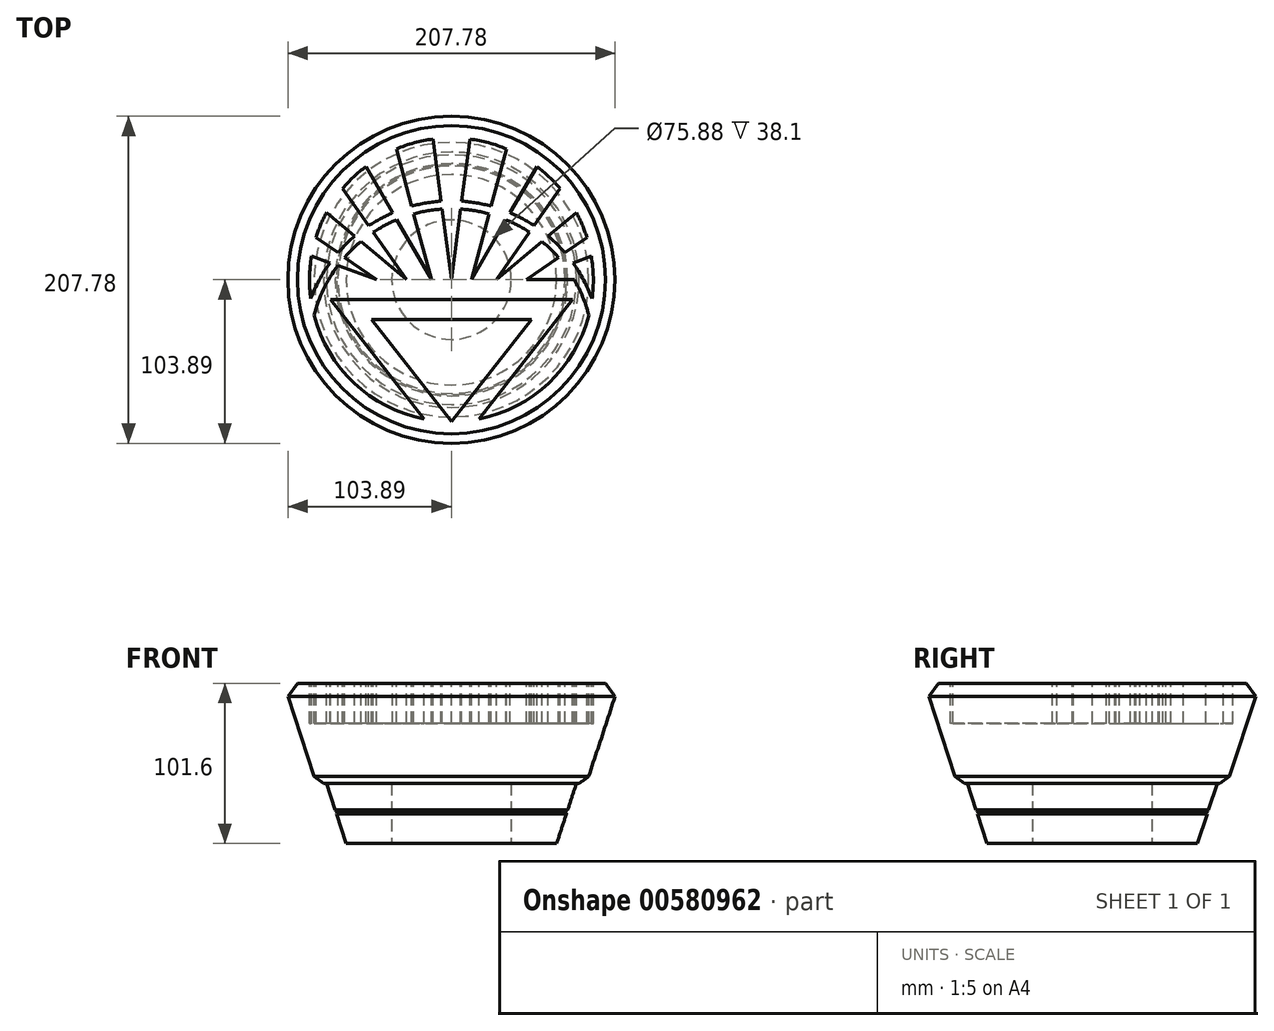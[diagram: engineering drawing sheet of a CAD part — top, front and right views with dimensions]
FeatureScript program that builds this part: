
annotation { "Feature Type Name" : "Feature", "Feature Type Description" : "" }
export const myFeature = defineFeature(function(context is Context, id is Id, definition is map)
    precondition{}
    {
        {
            var Q0;
            Q0=qCreatedBy(makeId("Top.planeOp"),FACE);
            var sketch = newSketch(context, id + "F0", { "sketchPlane" : qUnion([Q0])});
            skCircle(sketch, "E0", {"center": v(0, 0) * mm, "radius": 66.85 * mm});
            skSolve(sketch);
        }
        {
            var Q0;
            Q0=qCreatedBy(makeId("Top.planeOp"),FACE);
            cPlane(context, id + "F1", {"entities" : qUnion([Q0]), "cplaneType" : CPlaneType.OFFSET, "offset" : 101.6 * mm, "width" : 152.4 * mm, "height" : 152.4 * mm});
        }
        {
            var Q0;
            Q0=qCreatedBy(id+"F1.planeOp",FACE);
            var sketch = newSketch(context, id + "F2", { "sketchPlane" : qUnion([Q0])});
            skCircle(sketch, "E1", {"center": v(0, 0) * mm, "radius": 100.28 * mm});
            skSolve(sketch);
        }
        {
            var Q0;
            Q0=makeQuery(id+"F2.imprint","IMPRINT",FACE,{"disambiguationData":[TD([[makeQuery(id+"F2.imprint","IMPRINT",EDGE,{"derivedFrom":sQuery(id+"F2.wireOp",EDGE,"E1")}),1.0]])]});
            var Q1;
            Q1=makeQuery(id+"F0.imprint","IMPRINT",FACE,{"disambiguationData":[TD([[makeQuery(id+"F0.imprint","IMPRINT",EDGE,{"derivedFrom":sQuery(id+"F0.wireOp",EDGE,"E0")}),1.0]])]});
            var Q2;
            Q2=sQuery(id+"F2.wireOp",EDGE,"Eyu8YDiN-lEGU-Wuxt-0ncA-RZLAWeJK4OgB");
            var Q3;
            Q3=sQuery(id+"F0.wireOp",EDGE,"fgfE4CqQ-t5n6-ucAx-yhIW-5wF2yx0Jya2k");
            loft(context, id + "F3", {"sheetProfilesArray" : [{ "sheetProfileEntities" : qUnion([Q0]) }, { "sheetProfileEntities" : qUnion([Q1]) }], "wireProfilesArray" : [{ "wireProfileEntities" : qUnion([Q2]) }, { "wireProfileEntities" : qUnion([Q3]) }]});
        }
        {
            var Q0;
            Q0=qCreatedBy(makeId("Top.planeOp"),FACE);
            var sketch = newSketch(context, id + "F4", { "sketchPlane" : qUnion([Q0])});
            skCircle(sketch, "E2", {"center": v(0, 0) * mm, "radius": 37.94 * mm});
            skSolve(sketch);
        }
        {
            var Q0;
            Q0=makeQuery(id+"F4.imprint","IMPRINT",FACE,{"disambiguationData":[TD([[makeQuery(id+"F4.imprint","IMPRINT",EDGE,{"derivedFrom":sQuery(id+"F4.wireOp",EDGE,"E2")}),1.0]])]});
            extrude(context, id + "F5", {"entities" : qUnion([Q0]), "operationType" : NewBodyOperationType.REMOVE, "depth" : 53.34 * mm, "offsetDistance" : 25.4 * mm});
        }
        {
            var Q0;
            Q0=qCreatedBy(makeId("Top.planeOp"),FACE);
            cPlane(context, id + "F6", {"entities" : qUnion([Q0]), "cplaneType" : CPlaneType.OFFSET, "offset" : 38.1 * mm, "width" : 152.4 * mm, "height" : 152.4 * mm});
        }
        {
            var Q0;
            Q0=qCreatedBy(id+"F6.planeOp",FACE);
            var sketch = newSketch(context, id + "F7", { "sketchPlane" : qUnion([Q0])});
            skCircle(sketch, "E3", {"center": v(0, 0) * mm, "radius": 85.73 * mm});
            skSolve(sketch);
        }
        {
            var Q0;
            Q0=qCreatedBy(id+"F1.planeOp",FACE);
            var sketch = newSketch(context, id + "F8", { "sketchPlane" : qUnion([Q0])});
            skCircle(sketch, "E4", {"center": v(0, 0) * mm, "radius": 106.63 * mm});
            skSolve(sketch);
        }
        {
            var Q1;
            Q1=makeQuery(id+"F7.imprint","IMPRINT",FACE,{"disambiguationData":[TD([[makeQuery(id+"F7.imprint","IMPRINT",EDGE,{"derivedFrom":sQuery(id+"F7.wireOp",EDGE,"E3")}),1.0]])]});
            var Q2;
            Q2=makeQuery(id+"F8.imprint","IMPRINT",FACE,{"disambiguationData":[TD([[makeQuery(id+"F8.imprint","IMPRINT",EDGE,{"derivedFrom":sQuery(id+"F8.wireOp",EDGE,"E4")}),1.0]])]});
            loft(context, id + "F9", {"operationType" : NewBodyOperationType.ADD, "sheetProfilesArray" : [{ "sheetProfileEntities" : qUnion([Q1]) }, { "sheetProfileEntities" : qUnion([Q2]) }]});
        }
        {
            var Q0;
            Q0=makeQuery(id+"F9.opLoft","MID_CAP_EDGE",EDGE,{"disambiguationData":[OSD([sQuery(id+"F7.wireOp",EDGE,"E3")])],"capPos":0.0});
            chamfer(context, id + "F10", {"entities" : qUnion([Q0]), "width" : 6.35 * mm, "tangentPropagation" : true});
        }
        {
            var Q0;
            Q0=makeQuery(id+"F9.opLoft","MID_CAP_EDGE",EDGE,{"disambiguationData":[OSD([sQuery(id+"F7.wireOp",EDGE,"E3"),sQuery(id+"F8.wireOp",EDGE,"E4")])],"capPos":1.0});
            chamfer(context, id + "F11", {"entities" : qUnion([Q0]), "width" : 6.35 * mm, "tangentPropagation" : true});
        }
        {
            var Q0;
            Q0=qCreatedBy(makeId("Front.planeOp"),FACE);
            var sketch = newSketch(context, id + "F12", { "sketchPlane" : qUnion([Q0])});
            skLineSegment(sketch, "E5", {"start": v(-79.4, 38.11) * mm, "end": v(-66.85, 0) * mm});
            skLineSegment(sketch, "E6", {"start": v(-73.8, 21.14) * mm, "end": v(-72.2, 20.33) * mm});
            skLineSegment(sketch, "E7", {"start": v(-72.2, 20.33) * mm, "end": v(-73.02, 18.73) * mm});
            skSolve(sketch);
        }
        {
            var Q0;
            Q0=qCreatedBy(makeId("Right.planeOp"),FACE);
            var sketch = newSketch(context, id + "F13", { "sketchPlane" : qUnion([Q0])});
            skLineSegment(sketch, "E8", {"start": v(0, 0) * mm, "end": v(0, 184.2) * mm});
            skSolve(sketch);
        }
        {
            var Q0;
            Q0=qSketchRegion(id+"F12",true);
            var Q1;
            Q1=sQuery(id+"F13.wireOp",EDGE,"E8");
            revolve(context, id + "F14", {"operationType" : NewBodyOperationType.REMOVE, "entities" : qUnion([Q0]), "axis" : qUnion([Q1]), "revolveType" : RevolveType.FULL, "oppositeDirection" : true});
        }
        {
            var Q0;
            Q0=makeQuery(id+"F9.boolean.opBoolean","MERGE",FACE,{"derivedFrom":[makeQuery(id+"F3.opLoft","CAP_FACE",FACE,{"disambiguationData":[OSD([makeQuery(id+"F2.imprint","IMPRINT",FACE,{"disambiguationData":[TD([[makeQuery(id+"F2.imprint","IMPRINT",EDGE,{"derivedFrom":sQuery(id+"F2.wireOp",EDGE,"E1")}),1.0]])]})])],"isStart":true}),makeQuery(id+"F9.opLoft","CAP_FACE",FACE,{"disambiguationData":[OSD([makeQuery(id+"F8.imprint","IMPRINT",FACE,{"disambiguationData":[TD([[makeQuery(id+"F8.imprint","IMPRINT",EDGE,{"derivedFrom":sQuery(id+"F8.wireOp",EDGE,"E4")}),1.0]])]})])],"isStart":true})]});
            var sketch = newSketch(context, id + "F15", { "sketchPlane" : qUnion([Q0])});
            skCircle(sketch, "E9", {"center": v(0, 0) * mm, "radius": 100.28 * mm});
            skCircle(sketch, "E10.0", {"center": v(0, 0) * mm, "radius": 90.12 * mm});
            skLineSegment(sketch, "E11", {"start": v(0, 0) * mm, "end": v(0, 0) * mm});
            skLineSegment(sketch, "E12", {"start": v(0, -25.4) * mm, "end": v(-50.8, -25.4) * mm});
            skLineSegment(sketch, "E13", {"start": v(-50.8, -25.4) * mm, "end": v(0, -90.12) * mm});
            skLineSegment(sketch, "E14.0", {"start": v(-76.91, -12.7) * mm, "end": v(-17.49, -88.4) * mm});
            skLineSegment(sketch, "E14.1", {"start": v(0, -12.7) * mm, "end": v(-76.91, -12.7) * mm});
            skLineSegment(sketch, "E15.MirrorCS", {"start": v(0, -12.7) * mm, "end": v(76.91, -12.7) * mm});
            skLineSegment(sketch, "E16.MirrorCS", {"start": v(0, -25.4) * mm, "end": v(50.8, -25.4) * mm});
            skLineSegment(sketch, "E17.MirrorCS", {"start": v(50.8, -25.4) * mm, "end": v(0, -90.12) * mm});
            skLineSegment(sketch, "E18.MirrorCS", {"start": v(76.91, -12.7) * mm, "end": v(17.49, -88.4) * mm});
            skCircle(sketch, "E19", {"center": v(0, -45.06) * mm, "radius": 90.12 * mm});
            skLineSegment(sketch, "E20", {"start": v(0, 45.06) * mm, "end": v(0, 90.12) * mm});
            skLineSegment(sketch, "E21", {"start": v(0, 45.06) * mm, "end": v(0, 0) * mm});
            skLineSegment(sketch, "E22", {"start": v(0, 0) * mm, "end": v(0, -45.06) * mm});
            skCircle(sketch, "E23", {"center": v(0, -45.06) * mm, "radius": 95.2 * mm});
            skLineSegment(sketch, "E24", {"start": v(0, 0) * mm, "end": v(-11.76, 89.35) * mm});
            skLineSegment(sketch, "E25", {"start": v(0, 0) * mm, "end": v(11.76, 89.35) * mm});
            skLineSegment(sketch, "E26", {"start": v(-90.12, 0) * mm, "end": v(90.12, 0) * mm});
            skLineSegment(sketch, "E27", {"start": v(-12.7, 0) * mm, "end": v(-34.96, 83.06) * mm});
            skLineSegment(sketch, "E28", {"start": v(-12.7, 0) * mm, "end": v(-54.25, 71.96) * mm});
            skLineSegment(sketch, "E29", {"start": v(-28.57, 0) * mm, "end": v(-69.1, 57.86) * mm});
            skLineSegment(sketch, "E30", {"start": v(-28.58, 0) * mm, "end": v(-79.4, 42.64) * mm});
            skLineSegment(sketch, "E31", {"start": v(-47.62, 0) * mm, "end": v(-86.02, 26.88) * mm});
            skLineSegment(sketch, "E32", {"start": v(-47.62, 0) * mm, "end": v(-88.86, 15) * mm});
            skLineSegment(sketch, "E33.MirrorCS", {"start": v(12.7, 0) * mm, "end": v(34.96, 83.06) * mm});
            skLineSegment(sketch, "E34.MirrorCS", {"start": v(12.7, 0) * mm, "end": v(54.25, 71.96) * mm});
            skLineSegment(sketch, "E35.MirrorCS", {"start": v(28.57, 0) * mm, "end": v(69.1, 57.86) * mm});
            skLineSegment(sketch, "E36.MirrorCS", {"start": v(28.57, 0) * mm, "end": v(79.4, 42.64) * mm});
            skLineSegment(sketch, "E37.MirrorCS", {"start": v(47.62, 0) * mm, "end": v(86.02, 26.88) * mm});
            skLineSegment(sketch, "E38.MirrorCS", {"start": v(47.62, 0) * mm, "end": v(88.86, 15) * mm});
            skSolve(sketch);
        }
        {
            var Q0;
            Q0=makeQuery(id+"F15.imprint","IMPRINT",FACE,{"disambiguationData":[TD([[makeQuery(id+"F15.imprint","IMPRINT",EDGE,{"derivedFrom":sQuery(id+"F15.wireOp",EDGE,"E12")}),1.0]])]});
            var Q1;
            {var subQ6=sQuery(id+"F15.wireOp",EDGE,"E14.0");Q1=makeQuery(id+"F15.imprint","IMPRINT",FACE,{"disambiguationData":[TD([[makeQuery(id+"F15.imprint","IMPRINT",EDGE,{"derivedFrom":subQ6}),-1.0]])]});}
            var Q2;
            {var subQ5=sQuery(id+"F15.wireOp",EDGE,"E15.MirrorCS");Q2=makeQuery(id+"F15.imprint","IMPRINT",FACE,{"disambiguationData":[TD([[makeQuery(id+"F15.imprint","IMPRINT",EDGE,{"derivedFrom":subQ5}),1.0]])]});}
            var Q3;
            {var subQ0=sQuery(id+"F15.wireOp",EDGE,"E26");var subQ1=sQuery(id+"F15.wireOp",EDGE,"E10.0");var subQ2=makeQuery(id+"F15.imprint","INTERSECT",VERTEX,{"disambiguationData":[OD(0.0)],"derivedFrom":[subQ1,subQ0]});Q3=makeQuery(id+"F15.imprint","IMPRINT",FACE,{"disambiguationData":[TD([[makeQuery(id+"F15.imprint","IMPRINT",EDGE,{"disambiguationData":[TD([[subQ2,-1.0]])],"derivedFrom":subQ1}),1.0]])]});}
            var Q4;
            {var subQ0=sQuery(id+"F15.wireOp",EDGE,"E26");var subQ1=sQuery(id+"F15.wireOp",EDGE,"E10.0");var subQ2=makeQuery(id+"F15.imprint","INTERSECT",VERTEX,{"disambiguationData":[OD(0.0)],"derivedFrom":[subQ1,subQ0]});Q4=makeQuery(id+"F15.imprint","IMPRINT",FACE,{"disambiguationData":[TD([[makeQuery(id+"F15.imprint","IMPRINT",EDGE,{"disambiguationData":[TD([[subQ2,1.0]])],"derivedFrom":subQ1}),1.0]])]});}
            var Q5;
            {var subQ0=sQuery(id+"F15.wireOp",EDGE,"E32");var subQ1=sQuery(id+"F15.wireOp",EDGE,"E19");var subQ2=makeQuery(id+"F15.imprint","INTERSECT",VERTEX,{"derivedFrom":[subQ1,subQ0]});Q5=makeQuery(id+"F15.imprint","IMPRINT",FACE,{"disambiguationData":[TD([[makeQuery(id+"F15.imprint","IMPRINT",EDGE,{"disambiguationData":[TD([[subQ2,-1.0]])],"derivedFrom":subQ1}),1.0]])]});}
            var Q6;
            {var subQ0=sQuery(id+"F15.wireOp",EDGE,"E30");var subQ1=sQuery(id+"F15.wireOp",EDGE,"E19");var subQ2=makeQuery(id+"F15.imprint","INTERSECT",VERTEX,{"derivedFrom":[subQ1,subQ0]});Q6=makeQuery(id+"F15.imprint","IMPRINT",FACE,{"disambiguationData":[TD([[makeQuery(id+"F15.imprint","IMPRINT",EDGE,{"disambiguationData":[TD([[subQ2,-1.0]])],"derivedFrom":subQ1}),1.0]])]});}
            var Q7;
            {var subQ0=sQuery(id+"F15.wireOp",EDGE,"E30");var subQ1=sQuery(id+"F15.wireOp",EDGE,"E10.0");var subQ2=makeQuery(id+"F15.imprint","INTERSECT",VERTEX,{"derivedFrom":[subQ1,subQ0]});Q7=makeQuery(id+"F15.imprint","IMPRINT",FACE,{"disambiguationData":[TD([[makeQuery(id+"F15.imprint","IMPRINT",EDGE,{"disambiguationData":[TD([[subQ2,-1.0]])],"derivedFrom":subQ1}),1.0]])]});}
            var Q8;
            {var subQ0=sQuery(id+"F15.wireOp",EDGE,"E28");var subQ1=sQuery(id+"F15.wireOp",EDGE,"E10.0");var subQ2=makeQuery(id+"F15.imprint","INTERSECT",VERTEX,{"derivedFrom":[subQ1,subQ0]});Q8=makeQuery(id+"F15.imprint","IMPRINT",FACE,{"disambiguationData":[TD([[makeQuery(id+"F15.imprint","IMPRINT",EDGE,{"disambiguationData":[TD([[subQ2,-1.0]])],"derivedFrom":subQ1}),1.0]])]});}
            var Q9;
            {var subQ0=sQuery(id+"F15.wireOp",EDGE,"E28");var subQ1=sQuery(id+"F15.wireOp",EDGE,"E19");var subQ2=makeQuery(id+"F15.imprint","INTERSECT",VERTEX,{"derivedFrom":[subQ1,subQ0]});Q9=makeQuery(id+"F15.imprint","IMPRINT",FACE,{"disambiguationData":[TD([[makeQuery(id+"F15.imprint","IMPRINT",EDGE,{"disambiguationData":[TD([[subQ2,-1.0]])],"derivedFrom":subQ1}),1.0]])]});}
            var Q10;
            {var subQ0=sQuery(id+"F15.wireOp",EDGE,"E24");var subQ1=sQuery(id+"F15.wireOp",EDGE,"E10.0");var subQ2=makeQuery(id+"F15.imprint","INTERSECT",VERTEX,{"derivedFrom":[subQ1,subQ0]});Q10=makeQuery(id+"F15.imprint","IMPRINT",FACE,{"disambiguationData":[TD([[makeQuery(id+"F15.imprint","IMPRINT",EDGE,{"disambiguationData":[TD([[subQ2,-1.0]])],"derivedFrom":subQ1}),1.0]])]});}
            var Q11;
            {var subQ0=sQuery(id+"F15.wireOp",EDGE,"E24");var subQ1=sQuery(id+"F15.wireOp",EDGE,"E19");var subQ2=makeQuery(id+"F15.imprint","INTERSECT",VERTEX,{"derivedFrom":[subQ1,subQ0]});Q11=makeQuery(id+"F15.imprint","IMPRINT",FACE,{"disambiguationData":[TD([[makeQuery(id+"F15.imprint","IMPRINT",EDGE,{"disambiguationData":[TD([[subQ2,-1.0]])],"derivedFrom":subQ1}),1.0]])]});}
            var Q12;
            {var subQ0=sQuery(id+"F15.wireOp",EDGE,"E33.MirrorCS");var subQ1=sQuery(id+"F15.wireOp",EDGE,"E19");var subQ2=makeQuery(id+"F15.imprint","INTERSECT",VERTEX,{"derivedFrom":[subQ1,subQ0]});Q12=makeQuery(id+"F15.imprint","IMPRINT",FACE,{"disambiguationData":[TD([[makeQuery(id+"F15.imprint","IMPRINT",EDGE,{"disambiguationData":[TD([[subQ2,-1.0]])],"derivedFrom":subQ1}),1.0]])]});}
            var Q13;
            {var subQ0=sQuery(id+"F15.wireOp",EDGE,"E25");var subQ1=sQuery(id+"F15.wireOp",EDGE,"E10.0");var subQ2=makeQuery(id+"F15.imprint","INTERSECT",VERTEX,{"derivedFrom":[subQ1,subQ0]});Q13=makeQuery(id+"F15.imprint","IMPRINT",FACE,{"disambiguationData":[TD([[makeQuery(id+"F15.imprint","IMPRINT",EDGE,{"disambiguationData":[TD([[subQ2,1.0]])],"derivedFrom":subQ1}),1.0]])]});}
            var Q14;
            {var subQ0=sQuery(id+"F15.wireOp",EDGE,"E35.MirrorCS");var subQ1=sQuery(id+"F15.wireOp",EDGE,"E19");var subQ2=makeQuery(id+"F15.imprint","INTERSECT",VERTEX,{"derivedFrom":[subQ1,subQ0]});Q14=makeQuery(id+"F15.imprint","IMPRINT",FACE,{"disambiguationData":[TD([[makeQuery(id+"F15.imprint","IMPRINT",EDGE,{"disambiguationData":[TD([[subQ2,-1.0]])],"derivedFrom":subQ1}),1.0]])]});}
            var Q15;
            {var subQ0=sQuery(id+"F15.wireOp",EDGE,"E37.MirrorCS");var subQ1=sQuery(id+"F15.wireOp",EDGE,"E19");var subQ2=makeQuery(id+"F15.imprint","INTERSECT",VERTEX,{"derivedFrom":[subQ1,subQ0]});Q15=makeQuery(id+"F15.imprint","IMPRINT",FACE,{"disambiguationData":[TD([[makeQuery(id+"F15.imprint","IMPRINT",EDGE,{"disambiguationData":[TD([[subQ2,-1.0]])],"derivedFrom":subQ1}),1.0]])]});}
            var Q16;
            {var subQ0=sQuery(id+"F15.wireOp",EDGE,"E36.MirrorCS");var subQ1=sQuery(id+"F15.wireOp",EDGE,"E10.0");var subQ2=makeQuery(id+"F15.imprint","INTERSECT",VERTEX,{"derivedFrom":[subQ1,subQ0]});Q16=makeQuery(id+"F15.imprint","IMPRINT",FACE,{"disambiguationData":[TD([[makeQuery(id+"F15.imprint","IMPRINT",EDGE,{"disambiguationData":[TD([[subQ2,1.0]])],"derivedFrom":subQ1}),1.0]])]});}
            var Q17;
            {var subQ0=sQuery(id+"F15.wireOp",EDGE,"E26");var subQ1=sQuery(id+"F15.wireOp",EDGE,"E10.0");var subQ2=makeQuery(id+"F15.imprint","INTERSECT",VERTEX,{"disambiguationData":[OD(1.0)],"derivedFrom":[subQ1,subQ0]});Q17=makeQuery(id+"F15.imprint","IMPRINT",FACE,{"disambiguationData":[TD([[makeQuery(id+"F15.imprint","IMPRINT",EDGE,{"disambiguationData":[TD([[subQ2,-1.0]])],"derivedFrom":subQ1}),1.0]])]});}
            var Q18;
            {var subQ0=sQuery(id+"F15.wireOp",EDGE,"E26");var subQ1=sQuery(id+"F15.wireOp",EDGE,"E19");var subQ2=makeQuery(id+"F15.imprint","INTERSECT",VERTEX,{"disambiguationData":[OD(0.0)],"derivedFrom":[subQ1,subQ0]});Q18=makeQuery(id+"F15.imprint","IMPRINT",FACE,{"disambiguationData":[TD([[makeQuery(id+"F15.imprint","IMPRINT",EDGE,{"disambiguationData":[TD([[subQ2,-1.0]])],"derivedFrom":subQ1}),1.0]])]});}
            var Q19;
            {var subQ0=sQuery(id+"F15.wireOp",EDGE,"E26");var subQ1=sQuery(id+"F15.wireOp",EDGE,"E10.0");var subQ2=makeQuery(id+"F15.imprint","INTERSECT",VERTEX,{"disambiguationData":[OD(1.0)],"derivedFrom":[subQ1,subQ0]});Q19=makeQuery(id+"F15.imprint","IMPRINT",FACE,{"disambiguationData":[TD([[makeQuery(id+"F15.imprint","IMPRINT",EDGE,{"disambiguationData":[TD([[subQ2,1.0]])],"derivedFrom":subQ1}),1.0]])]});}
            var Q20;
            {var subQ0=sQuery(id+"F15.wireOp",EDGE,"E34.MirrorCS");var subQ1=sQuery(id+"F15.wireOp",EDGE,"E10.0");var subQ2=makeQuery(id+"F15.imprint","INTERSECT",VERTEX,{"derivedFrom":[subQ1,subQ0]});Q20=makeQuery(id+"F15.imprint","IMPRINT",FACE,{"disambiguationData":[TD([[makeQuery(id+"F15.imprint","IMPRINT",EDGE,{"disambiguationData":[TD([[subQ2,1.0]])],"derivedFrom":subQ1}),1.0]])]});}
            extrude(context, id + "F16", {"entities" : qUnion([Q0, Q1, Q2, Q3, Q4, Q5, Q6, Q7, Q8, Q9, Q10, Q11, Q12, Q13, Q14, Q15, Q16, Q17, Q18, Q19, Q20]), "operationType" : NewBodyOperationType.REMOVE, "oppositeDirection" : true, "depth" : 25.4 * mm, "offsetDistance" : 25.4 * mm});
        }
    });
